FCSTD DOCUMENT  (FreeCAD 1.0R39285 (Git))
Label: assembly
License: All rights reserved
LicenseURL: http://en.wikipedia.org/wiki/All_rights_reserved
objects: App::FeaturePython×7, App::Link×4, Assembly::JointGroup×1, Assembly::AssemblyObject×1
EXTERNAL_REF file=table_placeholder.FCStd obj=Body
EXTERNAL_REF file=Laptop_placeholder.FCStd obj=Body
EXTERNAL_REF file=laptop_riser.FCStd obj=Body

FEATURE [App::Link] table_body
  LinkedObject = -> <external table_placeholder.FCStd>#Body
FEATURE [App::FeaturePython] GroundedJoint  label="GroundedJoint_table"  # Assembly grounded joint (typed FeaturePython)
  ObjectToGround = -> table_body
FEATURE [App::Link] laptop_body
  LinkPlacement = pos=(-9.1e-15,-40.1258,15.2598) rot=(1,0,0;0.047835rad)
  LinkedObject = -> <external Laptop_placeholder.FCStd>#Body
  Placement = pos=(-9.1e-15,-40.1258,15.2598) rot=(1,0,0;0.047835rad)
FEATURE [App::Link] riser_body  label="riser_body_left"
  LinkPlacement = pos=(-6.3e-15,59.1358,10) rot=(0,0,1;3.14159rad)
  LinkedObject = -> <external laptop_riser.FCStd>#Body
  Placement = pos=(-6.3e-15,59.1358,10) rot=(0,0,1;3.14159rad)
FEATURE [App::Link] riser_body001  label="riser_body_right"
  LinkPlacement = pos=(158,109.596,10) rot=(0,0,1;3.14159rad)
  LinkedObject = -> <external laptop_riser.FCStd>#Body
  Placement = pos=(158,109.596,10) rot=(0,0,1;3.14159rad)
FEATURE [App::FeaturePython] Joint  label="Parallel_laptop on table"  # Assembly joint (typed FeaturePython)
  Activated = true
  AngleMax = 0
  AngleMin = 0
  Detach1 = false
  Detach2 = false
  Distance = 0
  Distance2 = 0
  EnableAngleMax = false
  EnableAngleMin = false
  EnableLengthMax = false
  EnableLengthMin = false
  JointType = 6 (Parallel)
  LengthMax = 0
  LengthMin = 0
  Placement1 = pos=(0,0,0) rot=(0,1,0;4.71239rad)
  Placement2 = pos=(0,0,0) rot=(0,1,0;4.71239rad)
  Reference1 = -> Assembly [table_body.Origin.YZ_Plane.,table_body.Origin.YZ_Plane.]
  Reference2 = -> Assembly [laptop_body.Origin.YZ_Plane.,laptop_body.Origin.YZ_Plane.]
FEATURE [App::FeaturePython] Joint001  label="Revolute_latop table angle"  # Assembly joint (typed FeaturePython)
  Activated = true
  AngleMax = 0
  AngleMin = 0
  Detach1 = false
  Detach2 = false
  Distance = 0
  Distance2 = 0
  EnableAngleMax = false
  EnableAngleMin = false
  EnableLengthMax = false
  EnableLengthMin = false
  JointType = 1 (Revolute)
  LengthMax = 0
  LengthMin = 0
  Placement1 = pos=(0,-150,10) rot=(0.707107,0,0.707107;3.14159rad)
  Placement2 = pos=(9.1e-15,-110,0) rot=(0.707107,0,0.707107;3.14159rad)
  Reference1 = -> Assembly [table_body.Edge12,table_body.Edge12]
  Reference2 = -> Assembly [laptop_body.Edge4,laptop_body.Edge4]
FEATURE [App::FeaturePython] Joint003  label="Distance_riser right on table"  # Assembly joint (typed FeaturePython)
  Activated = true
  AngleMax = 0
  AngleMin = 0
  Detach1 = false
  Detach2 = false
  Distance = 0
  Distance2 = 0
  EnableAngleMax = false
  EnableAngleMin = false
  EnableLengthMax = false
  EnableLengthMin = false
  JointType = 5 (Distance)
  LengthMax = 0
  LengthMin = 0
  Placement1 = pos=(0,-0.200375,3.08174) rot=(-0.707107,0,-0.707107;3.14159rad)
  Placement2 = pos=(-2.1e-15,2.7e-15,10) rot=(0,0,1;0rad)
  Reference1 = -> Assembly [riser_body001.Face10,riser_body001.Face10]
  Reference2 = -> Assembly [table_body.Face6,table_body.Face6]
FEATURE [App::FeaturePython] Joint004  label="Parallel002_riser left on laptop edge"  # Assembly joint (typed FeaturePython)
  Activated = true
  AngleMax = 0
  AngleMin = 0
  Detach1 = false
  Detach2 = false
  Distance = 0
  Distance2 = 0
  EnableAngleMax = false
  EnableAngleMin = false
  EnableLengthMax = false
  EnableLengthMin = false
  JointType = 6 (Parallel)
  LengthMax = 0
  LengthMin = 0
  Placement1 = pos=(10,-0.200375,3.08174) rot=(-0.707107,0,-0.707107;3.14159rad)
  Placement2 = pos=(-165,49.2977,40.3422) rot=(-0.707107,0,0.707107;3.14159rad)
  Reference1 = -> Assembly [riser_body.Face12,riser_body.Face12]
  Reference2 = -> Assembly [laptop_body.Face8,laptop_body.Face8]
FEATURE [App::FeaturePython] Joint005  label="Distance001_riser left on table"  # Assembly joint (typed FeaturePython)
  Activated = true
  AngleMax = 0
  AngleMin = 0
  Detach1 = false
  Detach2 = false
  Distance = 0
  Distance2 = 0
  EnableAngleMax = false
  EnableAngleMin = false
  EnableLengthMax = false
  EnableLengthMin = false
  JointType = 5 (Distance)
  LengthMax = 0
  LengthMin = 0
  Placement1 = pos=(-1.1e-15,-0.200375,3.08174) rot=(-0.707107,0,-0.707107;3.14159rad)
  Placement2 = pos=(-2.1e-15,2.7e-15,10) rot=(0,0,1;0rad)
  Reference1 = -> Assembly [riser_body.Face10,riser_body.Face10]
  Reference2 = -> Assembly [table_body.Face6,table_body.Face6]
FEATURE [App::FeaturePython] Joint006  label="Distance002_riser left and right close to laptop back"  # Assembly joint (typed FeaturePython)
  Activated = true
  AngleMax = 0
  AngleMin = 0
  Detach1 = false
  Detach2 = false
  Distance = 0
  Distance2 = 0
  EnableAngleMax = false
  EnableAngleMin = false
  EnableLengthMax = false
  EnableLengthMin = false
  JointType = 5 (Distance)
  LengthMax = 0
  LengthMin = 0
  Placement1 = pos=(0,0,0) rot=(1,0,0;1.5708rad)
  Placement2 = pos=(0,0,0) rot=(1,0,0;1.5708rad)
  Reference1 = -> Assembly [riser_body.Origin.XZ_Plane.,riser_body.Origin.XZ_Plane.]
  Reference2 = -> Assembly [riser_body001.Origin.XZ_Plane.,riser_body001.Origin.XZ_Plane.]
FEATURE [Assembly::JointGroup] Joints
  Group = -> [GroundedJoint,Joint,Joint001,Joint003,Joint004,Joint005,Joint006]
FEATURE [Assembly::AssemblyObject] Assembly
  Group = -> [Joints,table_body,GroundedJoint,laptop_body,riser_body,riser_body001,Joint,Joint001,Joint003,Joint004,Joint005,Joint006]
  Origin = -> Origin
  Type = Assembly

RESOLVED EXTERNAL PARTS (link-assembly join: the EXTERNAL_REF files above that resolve inside this repo's crawl, each included once):
---- part Laptop_placeholder.FCStd = doc fcstd_d789862a4ef9 ----
FCSTD DOCUMENT  (FreeCAD 1.0R39109 (Git))
Label: Laptop_placeholder
License: All rights reserved
LicenseURL: http://en.wikipedia.org/wiki/All_rights_reserved
objects: Sketcher::SketchObject×2, PartDesign::Pad×2, PartDesign::Body×1
note: 11 computed .brp shape members not serialized (recipe doc carries the construction recipe); baked Part::Feature solids carry a one-line shape summary decoded from their .brp

FEATURE [Sketcher::SketchObject] Sketch
  ArcFitTolerance = 1e-06
  AttachmentSupport = -> [XY_Plane]
  FullyConstrained = true
  MakeInternals = false
  MapMode = 5
  sketch-geometry (5):
    g0: LineSegment StartX=165 StartY=-110 StartZ=0 EndX=165 EndY=110 EndZ=0
    g1: LineSegment StartX=165 StartY=110 StartZ=0 EndX=-165 EndY=110 EndZ=0
    g2: LineSegment StartX=-165 StartY=110 StartZ=0 EndX=-165 EndY=-110 EndZ=0
    g3: LineSegment StartX=-165 StartY=-110 StartZ=0 EndX=165 EndY=-110 EndZ=0
    g4: GeomPoint [constr] X=0 Y=0 Z=0
  constraints (12):
    c: Coincident(g0,g1)
    c: Coincident(g1,g2)
    c: Coincident(g2,g3)
    c: Coincident(g3,g0)
    c: Vertical(g0)
    c: Vertical(g2)
    c: Horizontal(g1)
    c: Horizontal(g3)
    c: Symmetric(g2,g0,g4)
    c: Coincident(g4,g-1)
    c: DistanceX(g3,g3) = 330
    c: DistanceY(g0,g0) = 220
FEATURE [PartDesign::Pad] Pad
  Direction = (0,0,1)
  Length = 14
  Length2 = 10
  Profile = -> Sketch
  ReferenceAxis = -> Sketch [N_Axis]
  Refine = true
  Suppressed = false
  Type = 0
FEATURE [Sketcher::SketchObject] Sketch001
  ArcFitTolerance = 1e-06
  AttachmentSupport = -> [YZ_Plane]
  FullyConstrained = true
  MakeInternals = false
  MapMode = 5
  Placement = pos=(0,0,0) rot=(0.57735,0.57735,0.57735;2.0944rad)
  sketch-geometry (4):
    g0: LineSegment StartX=110 StartY=0 StartZ=0 EndX=181.824 EndY=197.335 EndZ=0
    g1: LineSegment StartX=174.307 StartY=200.072 StartZ=0 EndX=102.482 EndY=2.73616 EndZ=0
    g2: LineSegment StartX=181.824 StartY=197.335 StartZ=0 EndX=174.307 EndY=200.072 EndZ=0
    g3: LineSegment StartX=110 StartY=0 StartZ=0 EndX=102.482 EndY=2.73616 EndZ=0
  constraints (12):
    c: Distance(g0) = 210
    c: Angle(g-1,g0) = 1.22173
    c: PointOnObject(g0,g-1)
    c: Parallel(g0,g1)
    c: Distance(g1,g0) = 8
    c: Coincident(g2,g0)
    c: Coincident(g2,g1)
    c: Perpendicular(g1,g2)
    c: Equal(g0,g1)
    c: Coincident(g3,g0)
    c: Coincident(g3,g1)
    c: Distance(g0,g-2) = 110
FEATURE [PartDesign::Pad] Pad001
  BaseFeature = -> Pad
  Direction = (1,0,0)
  Length = 330
  Length2 = 10
  Midplane = true
  Profile = -> Sketch001
  ReferenceAxis = -> Sketch001 [N_Axis]
  Refine = true
  Suppressed = false
  Type = 0
FEATURE [PartDesign::Body] Body  label="laptop_body"
  AllowCompound = false
  Group = -> [Sketch,Pad,Sketch001,Pad001]
  Origin = -> Origin
  Tip = -> Pad001
---- part laptop_riser.FCStd = doc fcstd_62ace698593b ----
FCSTD DOCUMENT  (FreeCAD 1.0R39319 (Git))
Label: laptop_riser
License: All rights reserved
LicenseURL: http://en.wikipedia.org/wiki/All_rights_reserved
objects: Sketcher::SketchObject×1, PartDesign::Pad×1, PartDesign::Fillet×1, PartDesign::Chamfer×1, PartDesign::Body×1
note: 12 computed .brp shape members not serialized (recipe doc carries the construction recipe); baked Part::Feature solids carry a one-line shape summary decoded from their .brp

FEATURE [Sketcher::SketchObject] Sketch
  ArcFitTolerance = 1e-06
  AttachmentSupport = -> [YZ_Plane]
  FullyConstrained = true
  MakeInternals = false
  MapMode = 5
  Placement = pos=(0,0,0) rot=(0.57735,0.57735,0.57735;2.0944rad)
  sketch-geometry (32):
    g0: LineSegment [constr] StartX=20.8749 StartY=10 StartZ=0 EndX=0 EndY=11.094 EndZ=0
    g1: LineSegment StartX=0 StartY=0 StartZ=0 EndX=0 EndY=11.094 EndZ=0
    g2: LineSegment [constr] StartX=20.8749 StartY=10 StartZ=0 EndX=0 EndY=10 EndZ=0
    g3: LineSegment StartX=20.8749 StartY=10 StartZ=0 EndX=20 EndY=0 EndZ=0
    g4: LineSegment [constr] StartX=20 StartY=0 StartZ=0 EndX=20 EndY=10 EndZ=0
    g5: LineSegment [constr] StartX=20 StartY=10 StartZ=0 EndX=0 EndY=0 EndZ=0
    g6: LineSegment [constr] StartX=0 StartY=10 StartZ=0 EndX=20 EndY=0 EndZ=0
    g7: LineSegment StartX=0 StartY=0 StartZ=0 EndX=5.66667 EndY=0 EndZ=0
    g8: LineSegment [constr] StartX=5.66667 StartY=0 StartZ=0 EndX=5.66667 EndY=1.5 EndZ=0
    g9: LineSegment [constr] StartX=5.66667 StartY=1.5 StartZ=0 EndX=14.3333 EndY=1.5 EndZ=0
    g10: LineSegment [constr] StartX=14.3333 StartY=1.5 StartZ=0 EndX=14.3333 EndY=0 EndZ=0
    g11: LineSegment StartX=14.3333 StartY=0 StartZ=0 EndX=20 EndY=0 EndZ=0
    g12: LineSegment StartX=0 StartY=11.094 StartZ=0 EndX=5.66667 EndY=10.797 EndZ=0
    g13: LineSegment [constr] StartX=14.3333 StartY=8.84283 StartZ=0 EndX=14.3333 EndY=10.3428 EndZ=0
    g14: LineSegment StartX=14.3333 StartY=10.3428 StartZ=0 EndX=20.8749 EndY=10 EndZ=0
    g15: LineSegment [constr] StartX=5.66667 StartY=8.84283 StartZ=0 EndX=5.66667 EndY=5.17141 EndZ=0
    g16: LineSegment [constr] StartX=5.66667 StartY=1.5 StartZ=0 EndX=5.66667 EndY=5.17141 EndZ=0
    g17: LineSegment [constr] StartX=14.3333 StartY=8.84283 StartZ=0 EndX=14.3333 EndY=5.17141 EndZ=0
    g18: LineSegment [constr] StartX=14.3333 StartY=5.17141 StartZ=0 EndX=14.3333 EndY=1.5 EndZ=0
    g19: LineSegment [constr] StartX=5.66667 StartY=5.17141 StartZ=0 EndX=10 EndY=5.17141 EndZ=0
    g20: LineSegment [constr] StartX=10 StartY=5.17141 StartZ=0 EndX=14.3333 EndY=5.17141 EndZ=0
    g21: Circle CenterX=10 CenterY=5.17141 CenterZ=0 NormalX=0 NormalY=0 NormalZ=1 AngleXU=0 Radius=2.505
    g22: LineSegment [constr] StartX=5.66667 StartY=10.797 StartZ=0 EndX=5.66667 EndY=8.84283 EndZ=0
    g23: LineSegment [constr] StartX=5.66667 StartY=10.797 StartZ=0 EndX=5.58816 EndY=9.29908 EndZ=0
    g24: LineSegment [constr] StartX=5.58816 StartY=9.29908 StartZ=0 EndX=14.2548 EndY=8.84488 EndZ=0
    g25: LineSegment [constr] StartX=14.2548 StartY=8.84488 StartZ=0 EndX=14.3333 EndY=10.3428 EndZ=0
    g26: LineSegment StartX=5.66667 StartY=10.797 StartZ=0 EndX=7.08611 EndY=9.22058 EndZ=0
    g27: LineSegment StartX=7.08611 StartY=9.22058 StartZ=0 EndX=12.7569 EndY=8.92339 EndZ=0
    g28: LineSegment StartX=12.7569 StartY=8.92339 StartZ=0 EndX=14.3333 EndY=10.3428 EndZ=0
    g29: LineSegment StartX=5.66667 StartY=0 StartZ=0 EndX=7.16667 EndY=1.5 EndZ=0
    g30: LineSegment StartX=7.16667 StartY=1.5 StartZ=0 EndX=12.8333 EndY=1.5 EndZ=0
    g31: LineSegment StartX=12.8333 StartY=1.5 StartZ=0 EndX=14.3333 EndY=0 EndZ=0
  constraints (86):
    c: PointOnObject(g3,g-1)
    c: DistanceX(g1,g3) = 20
    c: Coincident(g1,g0)
    c: Vertical(g1)
    c: PointOnObject(g2,g1)
    c: Horizontal(g2)
    c: Angle(g0,g2) = 0.0523599
    c: Coincident(g2,g0)
    c: Coincident(g3,g0)
    c: PointOnObject(g4,g2)
    c: Vertical(g4)
    c: Angle(g3,g4) = 0.0872665
    c: Coincident(g5,g4)
    c: Coincident(g6,g2)
    c: DistanceY(g4,g4) = 10
    c: Coincident(g7,g1)
    c: PointOnObject(g7,g-1)
    c: Coincident(g8,g7)
    c: Coincident(g9,g8)
    c: Horizontal(g9)
    c: Coincident(g10,g9)
    c: PointOnObject(g10,g-1)
    c: Coincident(g11,g10)
    c: Coincident(g11,g3)
    c: Vertical(g8)
    c: Vertical(g10)
    c: Coincident(g1,g5)
    c: Coincident(g-1,g1)
    c: Distance(g7,g9) = 1.5
    c: Coincident(g12,g0)
    c: PointOnObject(g12,g0)
    c: PointOnObject(g13,g0)
    c: Coincident(g14,g13)
    c: Coincident(g14,g0)
    c: Vertical(g13)
    c: Equal(g13,g10)
    c: Coincident(g6,g3)
    c: Coincident(g4,g3)
    c: Coincident(g16,g8)
    c: Coincident(g16,g15)
    c: Vertical(g17)
    c: Coincident(g18,g17)
    c: Coincident(g18,g9)
    c: Vertical(g18)
    c: Vertical(g15)
    c: Vertical(g16)
    c: Equal(g16,g15)
    c: Equal(g15,g17)
    c: Coincident(g19,g15)
    c: Coincident(g20,g19)
    c: Coincident(g20,g17)
    c: Diameter(g21) = 5.01
    c: Coincident(g21,g19)
    c: Equal(g19,g20)
    c: Horizontal(g19)
    c: Coincident(g22,g12)
    c: Coincident(g22,g15)
    c: Vertical(g22)
    c: Horizontal(g20)
    c: Coincident(g17,g13)
    c: Coincident(g23,g12)
    c: Coincident(g24,g23)
    c: Coincident(g25,g24)
    c: Coincident(g25,g13)
    c: Perpendicular(g14,g25)
    c: Perpendicular(g25,g24)
    c: Perpendicular(g12,g23)
    c: Equal(g23,g8)
    c: Coincident(g26,g12)
    c: PointOnObject(g26,g24)
    c: Coincident(g27,g26)
    c: PointOnObject(g27,g24)
    c: Coincident(g28,g27)
    c: Coincident(g28,g13)
    c: Equal(g28,g26)
    c: Angle(g26,g24) = 0.785398
    c: Coincident(g29,g7)
    c: PointOnObject(g29,g9)
    c: Coincident(g30,g29)
    c: PointOnObject(g30,g9)
    c: Coincident(g31,g30)
    c: Coincident(g31,g10)
    c: Equal(g31,g29)
    c: Angle(g29,g8) = 0.785398
    c: Equal(g7,g30)
    c: Equal(g30,g11)
FEATURE [PartDesign::Pad] Pad
  Direction = (1,0,0)
  Length = 10
  Length2 = 10
  Placement = pos=(0,0,0) rot=(1,1,1;2.0944rad)
  Profile = -> Sketch
  ReferenceAxis = -> Sketch [N_Axis]
  Refine = true
  Suppressed = false
  Type = 0
FEATURE [PartDesign::Fillet] Fillet
  Base = -> Pad [Edge5,Edge8,Edge11,Edge14,Edge17,Edge20,Edge1,Edge2,Edge32,Edge29,Edge26,Edge23]
  BaseFeature = -> Pad
  Placement = pos=(0,0,0) rot=(1,1,1;2.0944rad)
  Radius = 1
  Refine = true
  SupportTransform = false
  Suppressed = false
  UseAllEdges = false
FEATURE [PartDesign::Chamfer] Chamfer
  Angle = 45
  Base = -> Fillet [Face2,Face5]
  BaseFeature = -> Fillet
  ChamferType = 0
  FlipDirection = false
  Placement = pos=(0,0,0) rot=(1,1,1;2.0944rad)
  Refine = true
  Size = 0.5
  Size2 = 1
  SupportTransform = false
  Suppressed = false
  UseAllEdges = false
FEATURE [PartDesign::Body] Body  label="riser_body"
  AllowCompound = false
  Group = -> [Sketch,Pad,Fillet,Chamfer]
  Origin = -> Origin
  Tip = -> Chamfer
---- part table_placeholder.FCStd = doc fcstd_8d4356c2bce3 ----
FCSTD DOCUMENT  (FreeCAD 1.0R39109 (Git))
Label: table_placeholder
License: All rights reserved
LicenseURL: http://en.wikipedia.org/wiki/All_rights_reserved
objects: Sketcher::SketchObject×1, PartDesign::Pad×1, PartDesign::Body×1
note: 6 computed .brp shape members not serialized (recipe doc carries the construction recipe); baked Part::Feature solids carry a one-line shape summary decoded from their .brp

FEATURE [Sketcher::SketchObject] Sketch
  ArcFitTolerance = 1e-06
  AttachmentSupport = -> [XY_Plane]
  FullyConstrained = true
  MakeInternals = false
  MapMode = 5
  sketch-geometry (5):
    g0: LineSegment StartX=250 StartY=-150 StartZ=0 EndX=250 EndY=150 EndZ=0
    g1: LineSegment StartX=250 StartY=150 StartZ=0 EndX=-250 EndY=150 EndZ=0
    g2: LineSegment StartX=-250 StartY=150 StartZ=0 EndX=-250 EndY=-150 EndZ=0
    g3: LineSegment StartX=-250 StartY=-150 StartZ=0 EndX=250 EndY=-150 EndZ=0
    g4: GeomPoint [constr] X=0 Y=0 Z=0
  constraints (12):
    c: Coincident(g0,g1)
    c: Coincident(g1,g2)
    c: Coincident(g2,g3)
    c: Coincident(g3,g0)
    c: Vertical(g0)
    c: Vertical(g2)
    c: Horizontal(g1)
    c: Horizontal(g3)
    c: Symmetric(g2,g0,g4)
    c: Coincident(g4,g-1)
    c: DistanceX(g3,g3) = 500
    c: DistanceY(g0,g0) = 300
FEATURE [PartDesign::Pad] Pad
  Direction = (0,0,1)
  Length = 10
  Length2 = 10
  Profile = -> Sketch
  ReferenceAxis = -> Sketch [N_Axis]
  Refine = true
  Suppressed = false
  Type = 0
FEATURE [PartDesign::Body] Body  label="table_body"
  AllowCompound = false
  Group = -> [Sketch,Pad]
  Origin = -> Origin
  Tip = -> Pad
